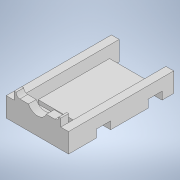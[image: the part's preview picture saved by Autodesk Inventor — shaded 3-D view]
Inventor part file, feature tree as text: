
AUTODESK INVENTOR PART (.ipt)
format: ipt  version: 2020.2 (Build 242310000, 310)  size: 196,608 bytes
history: native  units: mm
features: extrude x8, sketch x8, projected_geometry x3, plane x2
ambient origin geometry x8: Origin, YZ Plane, XZ Plane, XY Plane, X Axis, Y Axis, Z Axis, Center Point
bodies: Solid1 (feature_tree)
feature tree (21):
  extrude  "Extrusion1"  Depth=27.0mm
  extrude  "Extrusion2"  Depth=2.0mm
  extrude  "Extrusion3"  Depth=2.0mm
  extrude  "Extrusion4"  Depth=5.0mm
  plane  "Work Plane1"
  plane  "Work Plane2"
  extrude  "Extrusion5"  Depth=5.0mm
  extrude  "Extrusion6"  Depth=2.0mm
  extrude  "Extrusion7"  Depth=10.0mm TaperAngle=0.0deg
  extrude  "Extrusion8"  Depth=22.0mm
  sketch  "Sketch1"  dims[d0=16.0mm d1=27.0mm]
  sketch  "Sketch2"  dims[d2=2.0mm d3=0.0mm d4=2.0mm]
  sketch  "Sketch3"  dims[d5=2.0mm d6=2.0mm]
  projected_geometry  "Projected Loop1"
  sketch  "Sketch4"  dims[d7=3.0mm d8=0.0mm d9=5.0mm]
  sketch  "Sketch6"  dims[d10=5.0mm d11=9.0mm]
  sketch  "Sketch7"  dims[d12=2.0mm d13=2.0mm]
  projected_geometry  "Projected Loop2"
  projected_geometry  "Projected Loop3"
  sketch  "Sketch8"  dims[d14=2.0mm d15=0.0mm d16=10.0mm d17=0.0mm]
  sketch  "Sketch9"  dims[d18=7.0mm d19=22.0mm d22=2.0mm d23=45.0deg d24=3.6mm d25=0.0mm d26=3.6mm d27=0.0mm d28=22.5mm d29=10.0mm d30=0.0mm d31=1.0mm d32=3.2mm d33=1.0mm d34=0.0mm]
